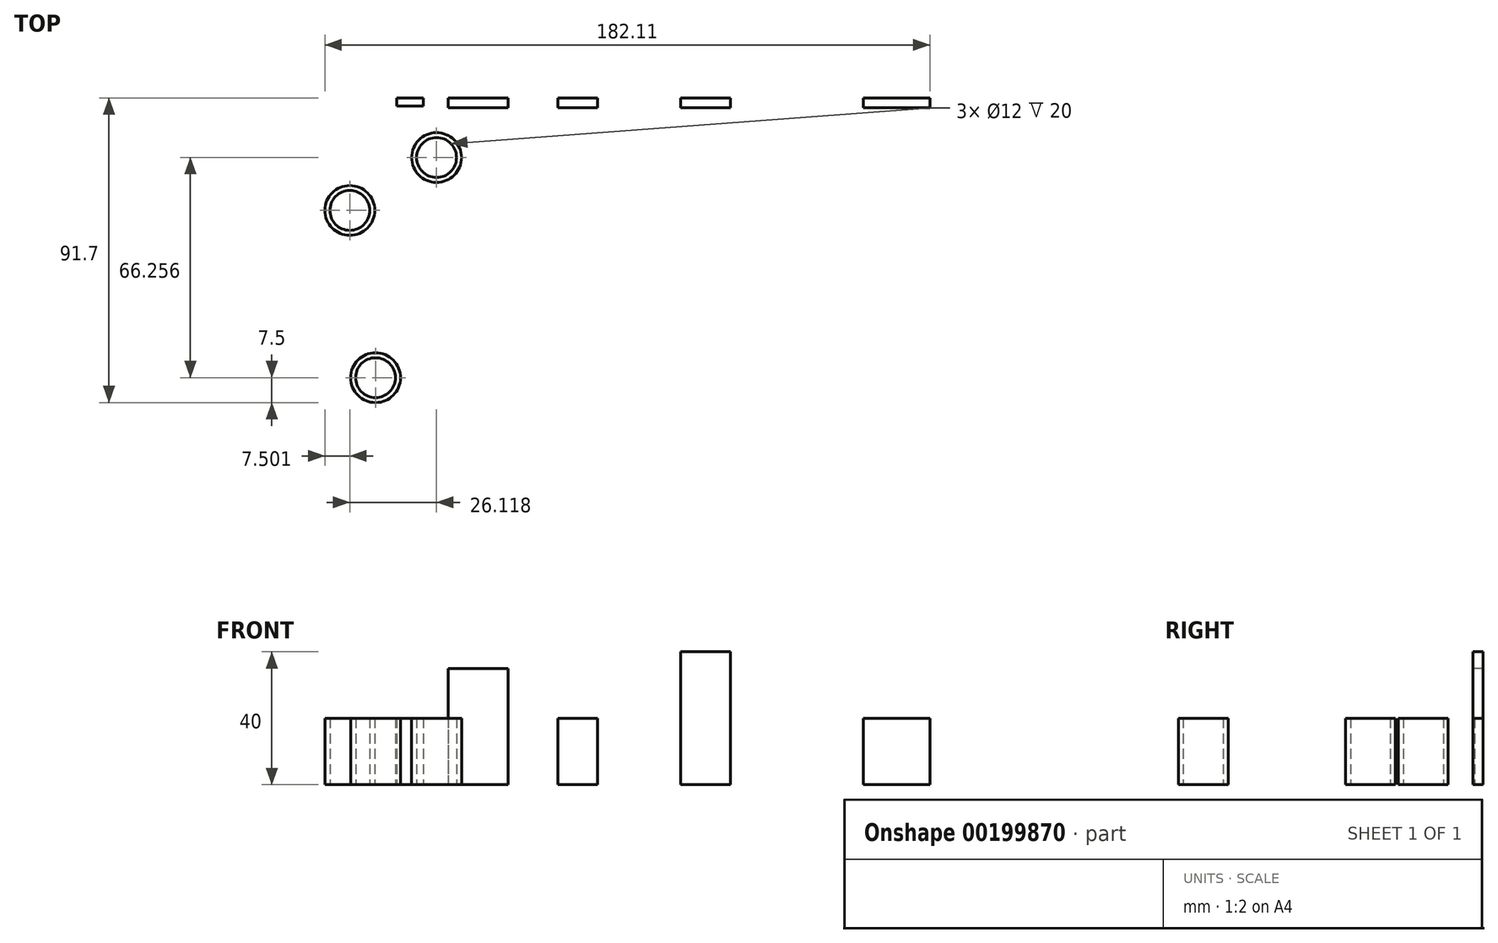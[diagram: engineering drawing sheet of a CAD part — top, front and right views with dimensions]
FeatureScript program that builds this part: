
annotation { "Feature Type Name" : "Feature", "Feature Type Description" : "" }
export const myFeature = defineFeature(function(context is Context, id is Id, definition is map)
    precondition{}
    {
        {
            var Q0;
            Q0=qCreatedBy(makeId("Top.planeOp"),FACE);
            var sketch = newSketch(context, id + "F0", { "sketchPlane" : qUnion([Q0])});
            skLineSegment(sketch, "E0.bottom", {"start": v(-51.37, 0) * mm, "end": v(-43.37, 0) * mm});
            skLineSegment(sketch, "E0.top", {"start": v(-51.37, -2.5) * mm, "end": v(-43.37, -2.5) * mm});
            skLineSegment(sketch, "E0.left", {"start": v(-51.37, 0) * mm, "end": v(-51.37, -2.5) * mm});
            skLineSegment(sketch, "E0.right", {"start": v(-43.37, 0) * mm, "end": v(-43.37, -2.5) * mm});
            skLineSegment(sketch, "E1.bottom", {"start": v(-35.87, 0) * mm, "end": v(-17.87, 0) * mm});
            skLineSegment(sketch, "E1.top", {"start": v(-35.87, -3) * mm, "end": v(-17.87, -3) * mm});
            skLineSegment(sketch, "E1.left", {"start": v(-35.87, 0) * mm, "end": v(-35.87, -3) * mm});
            skLineSegment(sketch, "E1.right", {"start": v(-17.87, 0) * mm, "end": v(-17.87, -3) * mm});
            skLineSegment(sketch, "E2.bottom", {"start": v(-2.87, 0) * mm, "end": v(9.13, 0) * mm});
            skLineSegment(sketch, "E2.top", {"start": v(-2.87, -3) * mm, "end": v(9.13, -3) * mm});
            skLineSegment(sketch, "E2.left", {"start": v(-2.87, 0) * mm, "end": v(-2.87, -3) * mm});
            skLineSegment(sketch, "E2.right", {"start": v(9.13, 0) * mm, "end": v(9.13, -3) * mm});
            skLineSegment(sketch, "E3.bottom", {"start": v(34.13, 0) * mm, "end": v(49.13, 0) * mm});
            skLineSegment(sketch, "E3.top", {"start": v(34.13, -3) * mm, "end": v(49.13, -3) * mm});
            skLineSegment(sketch, "E3.left", {"start": v(34.13, 0) * mm, "end": v(34.13, -3) * mm});
            skLineSegment(sketch, "E3.right", {"start": v(49.13, 0) * mm, "end": v(49.13, -3) * mm});
            skLineSegment(sketch, "E4.bottom", {"start": v(89.13, 0) * mm, "end": v(109.13, 0) * mm});
            skLineSegment(sketch, "E4.top", {"start": v(89.13, -3) * mm, "end": v(109.13, -3) * mm});
            skLineSegment(sketch, "E4.left", {"start": v(89.13, 0) * mm, "end": v(89.13, -3) * mm});
            skLineSegment(sketch, "E4.right", {"start": v(109.13, 0) * mm, "end": v(109.13, -3) * mm});
            skCircle(sketch, "E5", {"center": v(-39.36, -17.94) * mm, "radius": 7.5 * mm});
            skCircle(sketch, "E6", {"center": v(-39.36, -17.94) * mm, "radius": 6 * mm});
            skCircle(sketch, "E7", {"center": v(-65.48, -33.87) * mm, "radius": 7.5 * mm});
            skCircle(sketch, "E8", {"center": v(-65.48, -33.87) * mm, "radius": 6 * mm});
            skCircle(sketch, "E9", {"center": v(-57.72, -84.2) * mm, "radius": 7.5 * mm});
            skCircle(sketch, "E10", {"center": v(-57.72, -84.2) * mm, "radius": 6 * mm});
            skSolve(sketch);
        }
        {
            var Q0;
            Q0=makeQuery(id+"F0.imprint","IMPRINT",FACE,{"disambiguationData":[TD([[makeQuery(id+"F0.imprint","IMPRINT",EDGE,{"derivedFrom":sQuery(id+"F0.wireOp",EDGE,"E0.bottom")}),-1.0]])]});
            var Q1;
            Q1=makeQuery(id+"F0.imprint","IMPRINT",FACE,{"disambiguationData":[TD([[makeQuery(id+"F0.imprint","IMPRINT",EDGE,{"derivedFrom":sQuery(id+"F0.wireOp",EDGE,"E1.bottom")}),-1.0]])]});
            var Q2;
            Q2=makeQuery(id+"F0.imprint","IMPRINT",FACE,{"disambiguationData":[TD([[makeQuery(id+"F0.imprint","IMPRINT",EDGE,{"derivedFrom":sQuery(id+"F0.wireOp",EDGE,"E2.bottom")}),-1.0]])]});
            var Q3;
            Q3=makeQuery(id+"F0.imprint","IMPRINT",FACE,{"disambiguationData":[TD([[makeQuery(id+"F0.imprint","IMPRINT",EDGE,{"derivedFrom":sQuery(id+"F0.wireOp",EDGE,"E3.bottom")}),-1.0]])]});
            var Q4;
            Q4=makeQuery(id+"F0.imprint","IMPRINT",FACE,{"disambiguationData":[TD([[makeQuery(id+"F0.imprint","IMPRINT",EDGE,{"derivedFrom":sQuery(id+"F0.wireOp",EDGE,"E4.bottom")}),-1.0]])]});
            var Q5;
            Q5=makeQuery(id+"F0.imprint","IMPRINT",FACE,{"disambiguationData":[TD([[makeQuery(id+"F0.imprint","IMPRINT",EDGE,{"derivedFrom":sQuery(id+"F0.wireOp",EDGE,"E5")}),1.0]])]});
            var Q6;
            Q6=makeQuery(id+"F0.imprint","IMPRINT",FACE,{"disambiguationData":[TD([[makeQuery(id+"F0.imprint","IMPRINT",EDGE,{"derivedFrom":sQuery(id+"F0.wireOp",EDGE,"E9")}),1.0]])]});
            var Q7;
            Q7=makeQuery(id+"F0.imprint","IMPRINT",FACE,{"disambiguationData":[TD([[makeQuery(id+"F0.imprint","IMPRINT",EDGE,{"derivedFrom":sQuery(id+"F0.wireOp",EDGE,"E7")}),1.0]])]});
            extrude(context, id + "F1", {"entities" : qUnion([Q0, Q1, Q2, Q3, Q4, Q5, Q6, Q7]), "depth" : 20 * mm});
        }
        {
            var Q0;
            Q0=makeQuery(id+"F1.opExtrude","CAP_FACE",FACE,{"disambiguationData":[OSD([sQuery(id+"F0.wireOp",EDGE,"E1.bottom"),sQuery(id+"F0.wireOp",EDGE,"E1.top"),sQuery(id+"F0.wireOp",EDGE,"E1.left"),sQuery(id+"F0.wireOp",EDGE,"E1.right")])],"isStart":true});
            extrude(context, id + "F2", {"entities" : qUnion([Q0]), "operationType" : NewBodyOperationType.ADD, "oppositeDirection" : true, "depth" : 35 * mm});
        }
        {
            var Q0;
            Q0=makeQuery(id+"F1.opExtrude","CAP_FACE",FACE,{"disambiguationData":[OSD([sQuery(id+"F0.wireOp",EDGE,"E3.bottom"),sQuery(id+"F0.wireOp",EDGE,"E3.top"),sQuery(id+"F0.wireOp",EDGE,"E3.left"),sQuery(id+"F0.wireOp",EDGE,"E3.right")])],"isStart":true});
            extrude(context, id + "F3", {"entities" : qUnion([Q0]), "operationType" : NewBodyOperationType.ADD, "oppositeDirection" : true, "depth" : 40 * mm});
        }
    });
